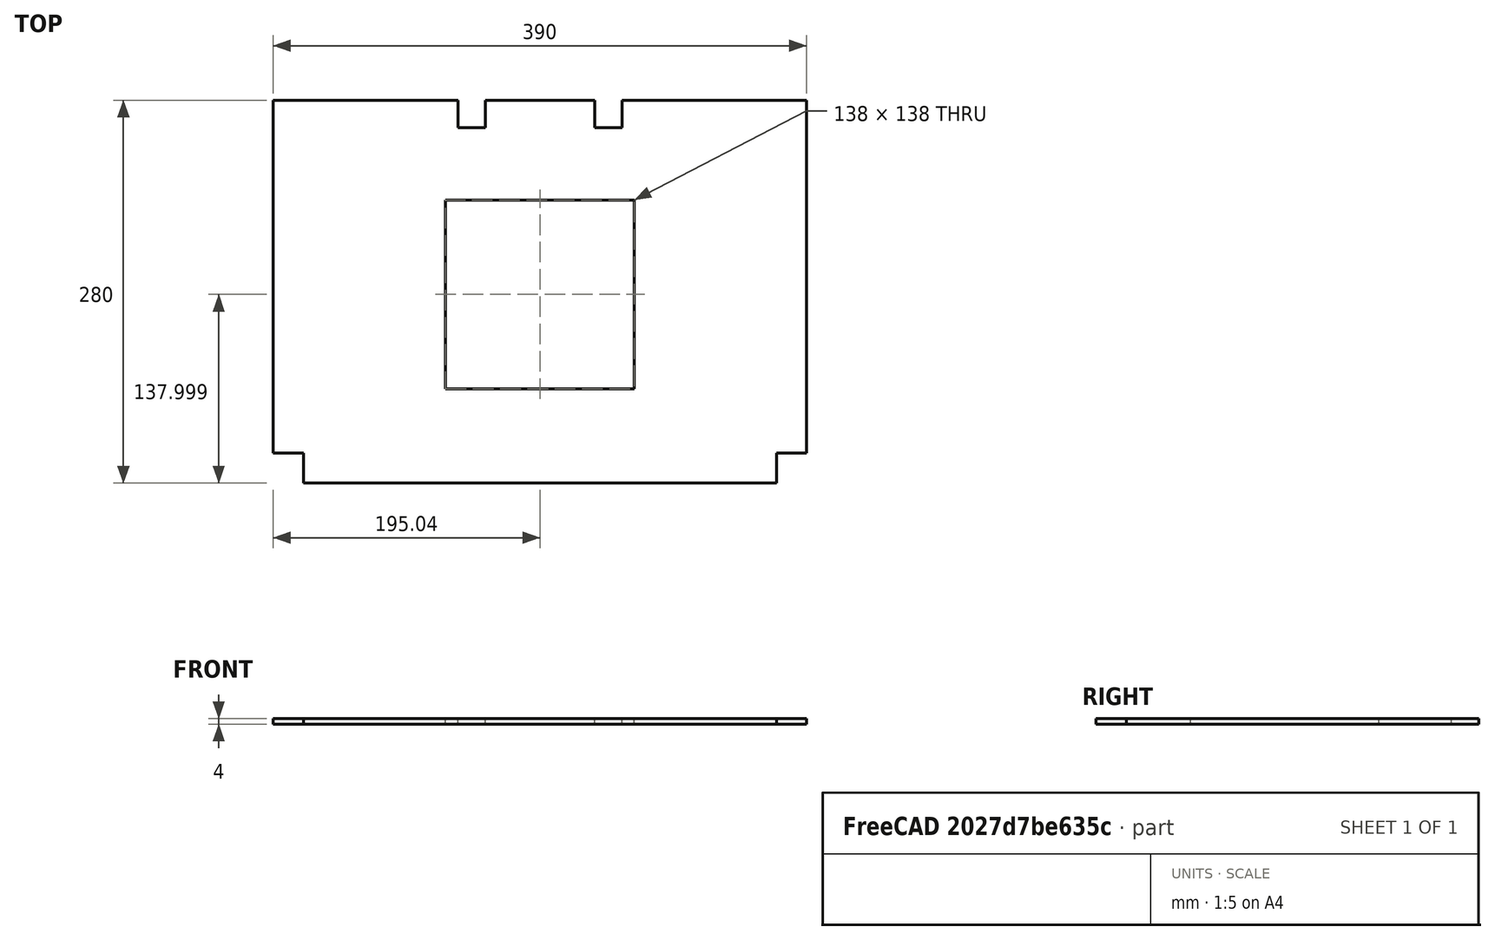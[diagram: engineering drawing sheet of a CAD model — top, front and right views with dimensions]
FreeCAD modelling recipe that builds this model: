
FCSTD DOCUMENT  (FreeCAD 0.14R3703 (Git))
Label: portacubeta
License: CC-BY 3.0
LicenseURL: http://creativecommons.org/licenses/by/3.0/
objects: Sketcher::SketchObject×1, PartDesign::Pad×1, Part::Feature×1
note: 4 computed .brp shape members not serialized (recipe doc carries the construction recipe); baked Part::Feature solids carry a one-line shape summary decoded from their .brp

FEATURE [Sketcher::SketchObject] Sketch
  sketch-geometry (20):
    g0: LineSegment StartX=-195.043 StartY=132.799 StartZ=0 EndX=-60.0432 EndY=132.799 EndZ=0
    g1: LineSegment StartX=-60.0432 StartY=132.799 StartZ=0 EndX=-60.0432 EndY=112.799 EndZ=0
    g2: LineSegment StartX=-60.0432 StartY=112.799 StartZ=0 EndX=-40.0432 EndY=112.799 EndZ=0
    g3: LineSegment StartX=-40.0432 StartY=112.799 StartZ=0 EndX=-40.0432 EndY=132.799 EndZ=0
    g4: LineSegment StartX=-40.0432 StartY=132.799 StartZ=0 EndX=39.9568 EndY=132.799 EndZ=0
    g5: LineSegment StartX=39.9568 StartY=132.799 StartZ=0 EndX=39.9568 EndY=112.799 EndZ=0
    g6: LineSegment StartX=39.9568 StartY=112.799 StartZ=0 EndX=59.9568 EndY=112.799 EndZ=0
    g7: LineSegment StartX=59.9568 StartY=112.799 StartZ=0 EndX=59.9568 EndY=132.799 EndZ=0
    g8: LineSegment StartX=59.9568 StartY=132.799 StartZ=0 EndX=194.957 EndY=132.799 EndZ=0
    g9: LineSegment StartX=194.957 StartY=132.799 StartZ=0 EndX=194.957 EndY=-125.201 EndZ=0
    g10: LineSegment StartX=194.957 StartY=-125.201 StartZ=0 EndX=172.957 EndY=-125.201 EndZ=0
    g11: LineSegment StartX=172.957 StartY=-125.201 StartZ=0 EndX=172.957 EndY=-147.201 EndZ=0
    g12: LineSegment StartX=172.957 StartY=-147.201 StartZ=0 EndX=-173.043 EndY=-147.201 EndZ=0
    g13: LineSegment StartX=-173.043 StartY=-147.201 StartZ=0 EndX=-173.043 EndY=-125.201 EndZ=0
    g14: LineSegment StartX=-173.043 StartY=-125.201 StartZ=0 EndX=-195.043 EndY=-125.201 EndZ=0
    g15: LineSegment StartX=-195.043 StartY=-125.201 StartZ=0 EndX=-195.043 EndY=132.799 EndZ=0
    g16: LineSegment StartX=-69 StartY=59.7988 StartZ=0 EndX=69 EndY=59.7988 EndZ=0
    g17: LineSegment StartX=69 StartY=59.7988 StartZ=0 EndX=69 EndY=-78.2012 EndZ=0
    g18: LineSegment StartX=69 StartY=-78.2012 StartZ=0 EndX=-69 EndY=-78.2012 EndZ=0
    g19: LineSegment StartX=-69 StartY=-78.2012 StartZ=0 EndX=-69 EndY=59.7988 EndZ=0
  constraints (60):
    c: Horizontal(g0)
    c: Coincident(g0,g1)
    c: Vertical(g1)
    c: Coincident(g1,g2)
    c: Horizontal(g2)
    c: Coincident(g2,g3)
    c: Vertical(g3)
    c: Coincident(g3,g4)
    c: Horizontal(g4)
    c: Coincident(g4,g5)
    c: Vertical(g5)
    c: Coincident(g5,g6)
    c: Horizontal(g6)
    c: Coincident(g6,g7)
    c: Vertical(g7)
    c: Coincident(g7,g8)
    c: Horizontal(g8)
    c: Vertical(g9)
    c: Coincident(g9,g10)
    c: Coincident(g11,g12)
    c: Horizontal(g12)
    c: Coincident(g12,g13)
    c: Vertical(g13)
    c: Coincident(g13,g14)
    c: Horizontal(g14)
    c: Coincident(g14,g15)
    c: Vertical(g15)
    c: Equal(g1,g3)
    c: Equal(g3,g5)
    c: Equal(g5,g7)
    c: Equal(g2,g6)
    c: DistanceY(g0,g12) = -280
    c: DistanceX(g0,g0) = 135
    c: DistanceX(g1,g2) = 20
    c: Equal(g2,g6)
    c: DistanceX(g3,g4) = 80
    c: Coincident(g11,g10)
    c: Vertical(g11)
    c: Horizontal(g10)
    c: DistanceY(g1,g0) = 20
    c: DistanceX(g12,g11) = 346
    c: DistanceX(g14,g13) = 22
    c: Equal(g14,g13)
    c: Equal(g14,g10)
    c: Equal(g10,g11)
    c: Coincident(g9,g8)
    c: Coincident(g15,g0)
    c: Equal(g6,g2)
    c: Coincident(g16,g17)
    c: Coincident(g17,g18)
    c: Coincident(g18,g19)
    c: Coincident(g19,g16)
    c: Horizontal(g16)
    c: Horizontal(g18)
    c: Vertical(g17)
    c: Vertical(g19)
    c: Symmetric(g18,g17,g-2)
    c: DistanceY(g17,g11) = -69
    c: DistanceY(g16,g17) = -138
    c: Equal(g17,g16)
FEATURE [PartDesign::Pad] Pad
  Length = 4
  Length2 = 10
  Sketch = -> Sketch
  Type = 0
FEATURE [Part::Feature] Pad001  label="portacubeta"
  shape: bbox 390 x 280 x 4 mm, 22 faces (baked)
